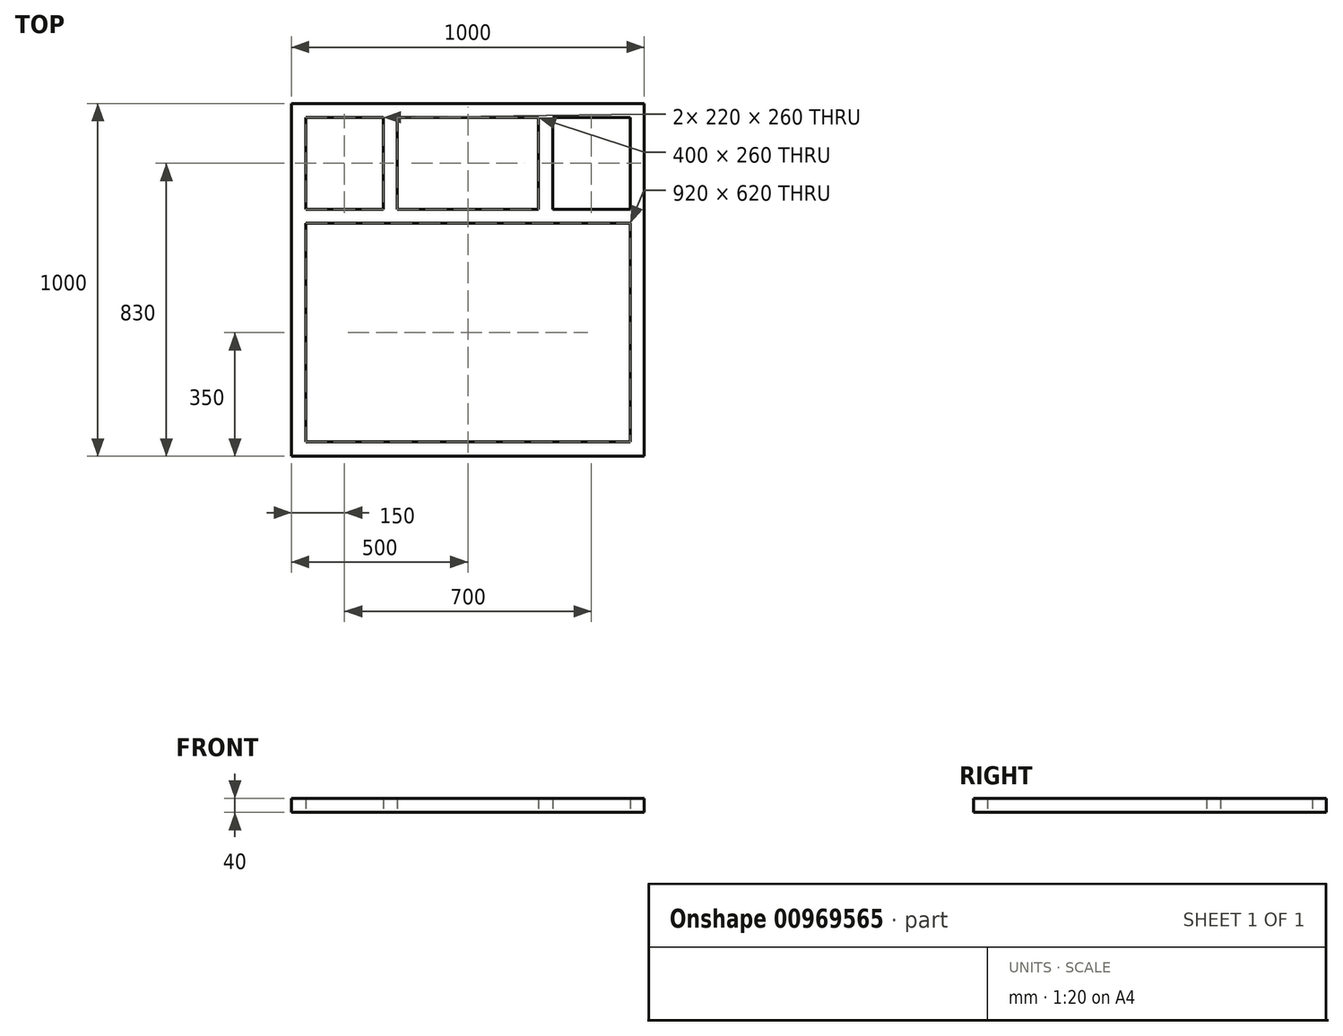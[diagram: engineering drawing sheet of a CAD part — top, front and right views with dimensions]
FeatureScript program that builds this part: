
annotation { "Feature Type Name" : "Feature", "Feature Type Description" : "" }
export const myFeature = defineFeature(function(context is Context, id is Id, definition is map)
    precondition{}
    {
        {
            var Q0;
            Q0=qCreatedBy(makeId("Top.planeOp"),FACE);
            var sketch = newSketch(context, id + "F0", { "sketchPlane" : qUnion([Q0])});
            skLineSegment(sketch, "E0.bottom", {"start": v(500, 500) * mm, "end": v(-500, 500) * mm});
            skLineSegment(sketch, "E0.top", {"start": v(500, -500) * mm, "end": v(-500, -500) * mm});
            skLineSegment(sketch, "E0.left", {"start": v(500, 500) * mm, "end": v(500, -500) * mm});
            skLineSegment(sketch, "E0.right", {"start": v(-500, 500) * mm, "end": v(-500, -500) * mm});
            skPoint(sketch, "E0.middle", {"position": v(0, 0) * mm});
            skLineSegment(sketch, "E1.0", {"start": v(460, 460) * mm, "end": v(-460, 460) * mm});
            skLineSegment(sketch, "E1.1", {"start": v(460, 460) * mm, "end": v(460, -460) * mm});
            skLineSegment(sketch, "E1.2", {"start": v(460, -460) * mm, "end": v(-460, -460) * mm});
            skLineSegment(sketch, "E1.3", {"start": v(-460, 460) * mm, "end": v(-460, -460) * mm});
            skSolve(sketch);
        }
        {
            var Q0;
            Q0 = qSketchRegion(id + "F0", true);
            extrude(context, id + "F1", {"entities" : qUnion([Q0]), "depth" : 40 * mm, "offsetDistance" : 25 * mm});
        }
        {
            var Q0;
            Q0=qCreatedBy(makeId("Top.planeOp"),FACE);
            var sketch = newSketch(context, id + "F2", { "sketchPlane" : qUnion([Q0])});
            skLineSegment(sketch, "E2.bottom", {"start": v(-460, 160) * mm, "end": v(460, 160) * mm});
            skLineSegment(sketch, "E2.top", {"start": v(-460, 200) * mm, "end": v(-240, 200) * mm});
            skLineSegment(sketch, "E2.left", {"start": v(-460, 200) * mm, "end": v(-460, 160) * mm});
            skLineSegment(sketch, "E2.right", {"start": v(460, 200) * mm, "end": v(460, 160) * mm});
            skLineSegment(sketch, "E3.bottom", {"start": v(-240, 460) * mm, "end": v(-200, 460) * mm});
            skLineSegment(sketch, "E3.left", {"start": v(-240, 460) * mm, "end": v(-240, 200) * mm});
            skLineSegment(sketch, "E3.right", {"start": v(-200, 460) * mm, "end": v(-200, 200) * mm});
            skLineSegment(sketch, "E4.bottom", {"start": v(240, 460) * mm, "end": v(200, 460) * mm});
            skLineSegment(sketch, "E4.left", {"start": v(240, 460) * mm, "end": v(240, 200) * mm});
            skLineSegment(sketch, "E4.right", {"start": v(200, 460) * mm, "end": v(200, 200) * mm});
            skLineSegment(sketch, "E5", {"start": v(0, 460) * mm, "end": v(0, 200) * mm, "construction": true});
            skLineSegment(sketch, "E6.trimOffspring", {"start": v(-200, 200) * mm, "end": v(200, 200) * mm});
            skLineSegment(sketch, "E7.trimOffspring", {"start": v(240, 200) * mm, "end": v(460, 200) * mm});
            skSolve(sketch);
        }
        {
            var Q0;
            Q0 = qSketchRegion(id + "F2", true);
            extrude(context, id + "F3", {"entities" : qUnion([Q0]), "operationType" : NewBodyOperationType.ADD, "depth" : 40 * mm, "offsetDistance" : 25 * mm});
        }
    });
